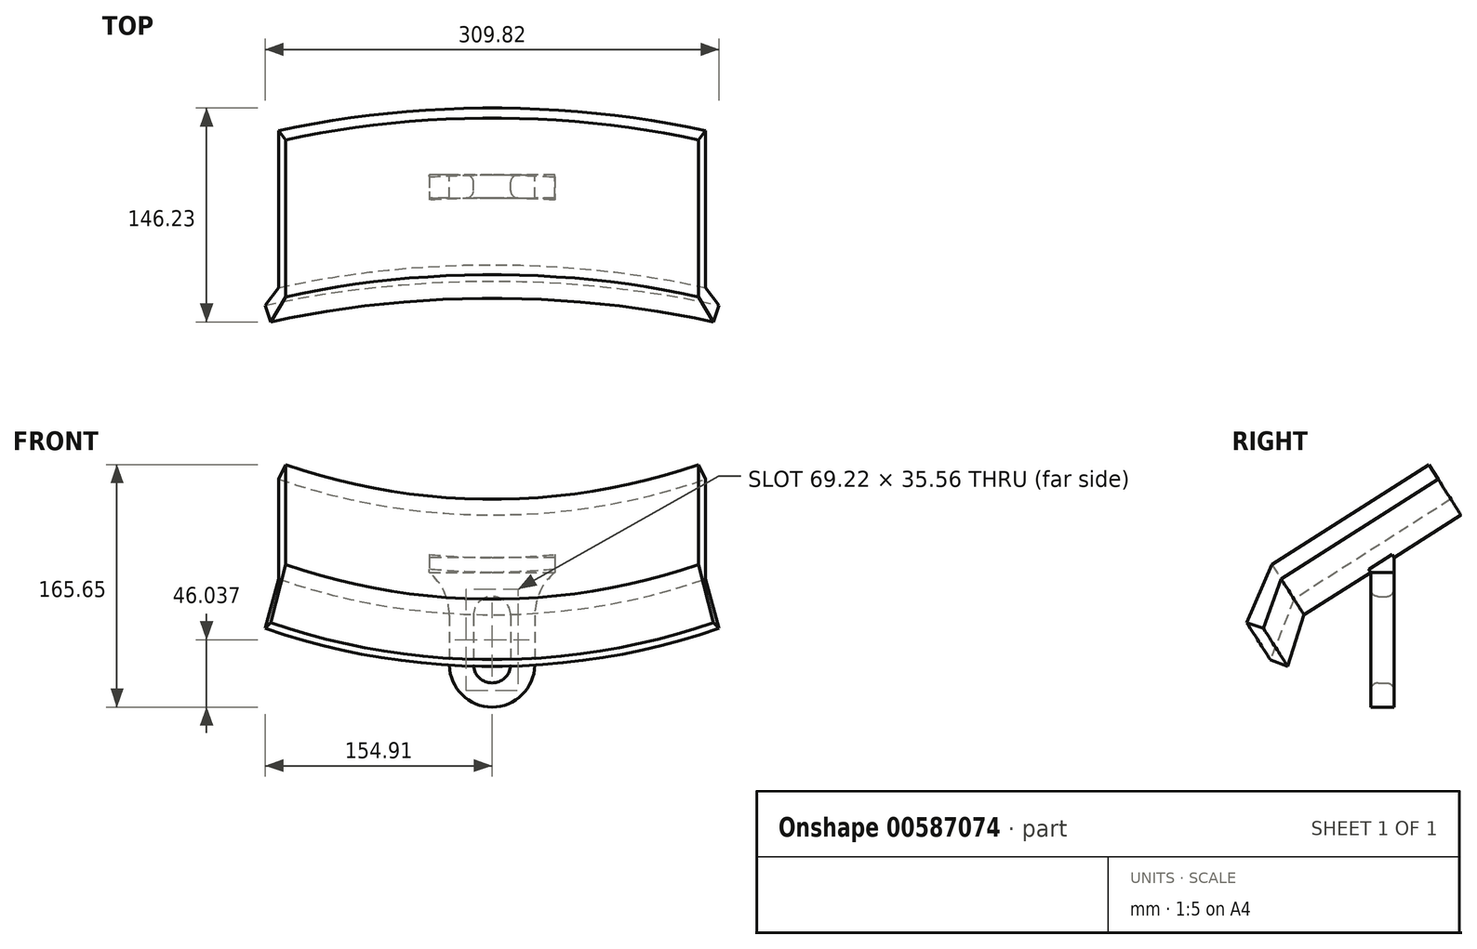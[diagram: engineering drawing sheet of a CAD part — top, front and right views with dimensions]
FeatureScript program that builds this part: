
annotation { "Feature Type Name" : "Feature", "Feature Type Description" : "" }
export const myFeature = defineFeature(function(context is Context, id is Id, definition is map)
    precondition{}
    {
        {
            var Q0;
            Q0=qCreatedBy(makeId("Front.planeOp"),FACE);
            var sketch = newSketch(context, id + "F0", { "sketchPlane" : qUnion([Q0])});
            skArc(sketch, "E0", {"start": v(-12.7, -67.31) * mm, "mid": v(0, -80.01) * mm, "end": v(12.7, -67.31) * mm});
            skArc(sketch, "E1", {"start": v(12.7, -33.66) * mm, "mid": v(0, -20.96) * mm, "end": v(-12.7, -33.66) * mm});
            skLineSegment(sketch, "E2", {"start": v(12.7, -33.66) * mm, "end": v(12.7, -67.31) * mm});
            skLineSegment(sketch, "E3", {"start": v(-12.7, -33.66) * mm, "end": v(-12.7, -67.31) * mm});
            skPoint(sketch, "E4.center.orphan", {"position": v(0, 0) * mm});
            skArc(sketch, "E5.0", {"start": v(-29.2, -67.31) * mm, "mid": v(0, -96.52) * mm, "end": v(29.2, -67.31) * mm});
            skLineSegment(sketch, "E5.1", {"start": v(-29.2, -33.66) * mm, "end": v(-29.2, -67.31) * mm});
            skLineSegment(sketch, "E5.3", {"start": v(29.2, -33.66) * mm, "end": v(29.2, -67.31) * mm});
            skLineSegment(sketch, "E6", {"start": v(-42.85, -4.45) * mm, "end": v(42.85, -4.45) * mm});
            skPoint(sketch, "E6.startSnap0", {"position": v(0, -4.45) * mm});
            skArc(sketch, "E7", {"start": v(-29.2, -33.66) * mm, "mid": v(-32.79, -17.54) * mm, "end": v(-42.85, -4.45) * mm});
            skArc(sketch, "E8", {"start": v(42.85, -4.45) * mm, "mid": v(32.79, -17.54) * mm, "end": v(29.2, -33.66) * mm});
            skSolve(sketch);
        }
        {
            var Q0;
            Q0=makeQuery(id+"F0.imprint","IMPRINT",FACE,{"disambiguationData":[TD([[makeQuery(id+"F0.imprint","IMPRINT",EDGE,{"derivedFrom":sQuery(id+"F0.wireOp",EDGE,"E0")}),-1.0]])]});
            extrude(context, id + "F1", {"entities" : qUnion([Q0]), "depth" : 15.88 * mm, "offsetDistance" : 25.4 * mm});
        }
        {
            var Q0;
            Q0=qCreatedBy(makeId("Right.planeOp"),FACE);
            var sketch = newSketch(context, id + "F2", { "sketchPlane" : qUnion([Q0])});
            skLineSegment(sketch, "E9", {"start": v(-15.87, -4.45) * mm, "end": v(0, 5.66) * mm});
            skLineSegment(sketch, "E10", {"start": v(0, 5.66) * mm, "end": v(0, -4.45) * mm});
            skLineSegment(sketch, "E11", {"start": v(0, -4.45) * mm, "end": v(-15.88, -4.45) * mm});
            skSolve(sketch);
        }
        {
            var Q0;
            Q0=qSketchRegion(id+"F2",true);
            extrude(context, id + "F3", {"entities" : qUnion([Q0]), "operationType" : NewBodyOperationType.ADD, "endBound" : BoundingType.SYMMETRIC, "depth" : 85.69 * mm, "offsetDistance" : 25.4 * mm});
        }
        {
            var Q0;
            Q0=makeQuery(id+"F1.opExtrude","CAP_EDGE",EDGE,{"disambiguationData":[OSD([sQuery(id+"F0.wireOp",EDGE,"E3")])],"isStart":false});
            fillet(context, id + "F4", {"entities" : qUnion([Q0]), "radius" : 5.08 * mm, "tangentPropagation" : true, "allowEdgeOverflow" : false});
        }
        {
            var Q0;
            Q0=makeQuery(id+"F1.opExtrude","CAP_EDGE",EDGE,{"disambiguationData":[OSD([sQuery(id+"F0.wireOp",EDGE,"E1")])],"isStart":true});
            fillet(context, id + "F5", {"entities" : qUnion([Q0]), "radius" : 5.08 * mm, "tangentPropagation" : true, "allowEdgeOverflow" : false});
        }
        {
            var Q0;
            Q0=makeQuery(id+"F1.opExtrude","SWEPT_BODY",BODY,{"disambiguationData":[OSD([sQuery(id+"F0.wireOp",EDGE,"E0"),sQuery(id+"F0.wireOp",EDGE,"E1"),sQuery(id+"F0.wireOp",EDGE,"E2"),sQuery(id+"F0.wireOp",EDGE,"E3"),sQuery(id+"F0.wireOp",EDGE,"E5.0"),sQuery(id+"F0.wireOp",EDGE,"E5.1"),sQuery(id+"F0.wireOp",EDGE,"E5.3"),sQuery(id+"F0.wireOp",EDGE,"E6"),sQuery(id+"F0.wireOp",EDGE,"E7"),sQuery(id+"F0.wireOp",EDGE,"E8")])]});
            transform(context, id + "F6", {"entities" : qUnion([Q0]), "transformType" : TransformType.TRANSLATION_3D, "dx" : 0 * mm, "dy" : 0 * mm, "dz" : -92.46 * mm, "makeCopy" : true});
        }
        {
            var Q0;
            Q0=makeQuery(id+"F1.opExtrude","SWEPT_BODY",BODY,{"disambiguationData":[OSD([sQuery(id+"F0.wireOp",EDGE,"E0"),sQuery(id+"F0.wireOp",EDGE,"E1"),sQuery(id+"F0.wireOp",EDGE,"E2"),sQuery(id+"F0.wireOp",EDGE,"E3"),sQuery(id+"F0.wireOp",EDGE,"E5.0"),sQuery(id+"F0.wireOp",EDGE,"E5.1"),sQuery(id+"F0.wireOp",EDGE,"E5.3"),sQuery(id+"F0.wireOp",EDGE,"E6"),sQuery(id+"F0.wireOp",EDGE,"E7"),sQuery(id+"F0.wireOp",EDGE,"E8")])]});
            transform(context, id + "F7", {"entities" : qUnion([Q0]), "transformType" : TransformType.TRANSLATION_3D, "dx" : 0 * mm, "dy" : 0 * mm, "dz" : -34.8 * mm, "makeCopy" : true});
        }
        {
            var Q0;
            Q0=makeQuery(id+"F7.opPattern","COPY",BODY,{"derivedFrom":makeQuery(id+"F1.opExtrude","SWEPT_BODY",BODY,{"disambiguationData":[OSD([sQuery(id+"F0.wireOp",EDGE,"E0"),sQuery(id+"F0.wireOp",EDGE,"E1"),sQuery(id+"F0.wireOp",EDGE,"E2"),sQuery(id+"F0.wireOp",EDGE,"E3"),sQuery(id+"F0.wireOp",EDGE,"E5.0"),sQuery(id+"F0.wireOp",EDGE,"E5.1"),sQuery(id+"F0.wireOp",EDGE,"E5.3"),sQuery(id+"F0.wireOp",EDGE,"E6"),sQuery(id+"F0.wireOp",EDGE,"E7"),sQuery(id+"F0.wireOp",EDGE,"E8")])]}),"instanceName":"1"});
            deleteBodies(context, id + "F8", {"entities" : qUnion([Q0])});
        }
        {
            var Q0;
            Q0=qCreatedBy(makeId("Right.planeOp"),FACE);
            var sketch = newSketch(context, id + "F9", { "sketchPlane" : qUnion([Q0])});
            skLineSegment(sketch, "E12", {"start": v(45.71, 34.77) * mm, "end": v(-61.41, -33.44) * mm});
            skLineSegment(sketch, "E13", {"start": v(-61.41, -33.44) * mm, "end": v(-68.24, -22.73) * mm});
            skLineSegment(sketch, "E14", {"start": v(-68.24, -22.73) * mm, "end": v(38.9, 45.48) * mm});
            skLineSegment(sketch, "E15", {"start": v(38.9, 45.48) * mm, "end": v(45.71, 34.77) * mm});
            skLineSegment(sketch, "E16", {"start": v(-61.41, -33.44) * mm, "end": v(-266.04, 287.95) * mm});
            skLineSegment(sketch, "E17", {"start": v(-266.04, 287.95) * mm, "end": v(-161.06, 354.79) * mm});
            skLineSegment(sketch, "E18", {"start": v(-68.24, -22.73) * mm, "end": v(-84.4, -64.14) * mm});
            skLineSegment(sketch, "E19", {"start": v(-84.4, -64.14) * mm, "end": v(-72.56, -68.75) * mm});
            skLineSegment(sketch, "E20", {"start": v(-72.56, -68.75) * mm, "end": v(-61.41, -33.44) * mm});
            skSolve(sketch);
        }
        {
            var Q0;
            Q0=qSketchRegion(id+"F9",true);
            var Q1;
            Q1=sQuery(id+"F9.wireOp",EDGE,"E17");
            revolve(context, id + "F10", {"operationType" : NewBodyOperationType.ADD, "entities" : qUnion([Q0]), "axis" : qUnion([Q1]), "revolveType" : RevolveType.SYMMETRIC, "angle" : 45 * degree});
        }
        {
            var Q0;
            Q0=makeQuery(id+"F6.opPattern","COPY",BODY,{"derivedFrom":makeQuery(id+"F1.opExtrude","SWEPT_BODY",BODY,{"disambiguationData":[OSD([sQuery(id+"F0.wireOp",EDGE,"E0"),sQuery(id+"F0.wireOp",EDGE,"E1"),sQuery(id+"F0.wireOp",EDGE,"E2"),sQuery(id+"F0.wireOp",EDGE,"E3"),sQuery(id+"F0.wireOp",EDGE,"E5.0"),sQuery(id+"F0.wireOp",EDGE,"E5.1"),sQuery(id+"F0.wireOp",EDGE,"E5.3"),sQuery(id+"F0.wireOp",EDGE,"E6"),sQuery(id+"F0.wireOp",EDGE,"E7"),sQuery(id+"F0.wireOp",EDGE,"E8")])]}),"instanceName":"1"});
            deleteBodies(context, id + "F11", {"entities" : qUnion([Q0])});
        }
        {
            var Q0;
            Q0=makeQuery(id+"F3.opExtrude","SWEPT_FACE",FACE,{"disambiguationData":[OSD([sQuery(id+"F2.wireOp",EDGE,"E9")])]});
            extrude(context, id + "F12", {"entities" : qUnion([Q0]), "operationType" : NewBodyOperationType.ADD, "depth" : 6.35 * mm, "offsetDistance" : 25.4 * mm});
        }
    });
